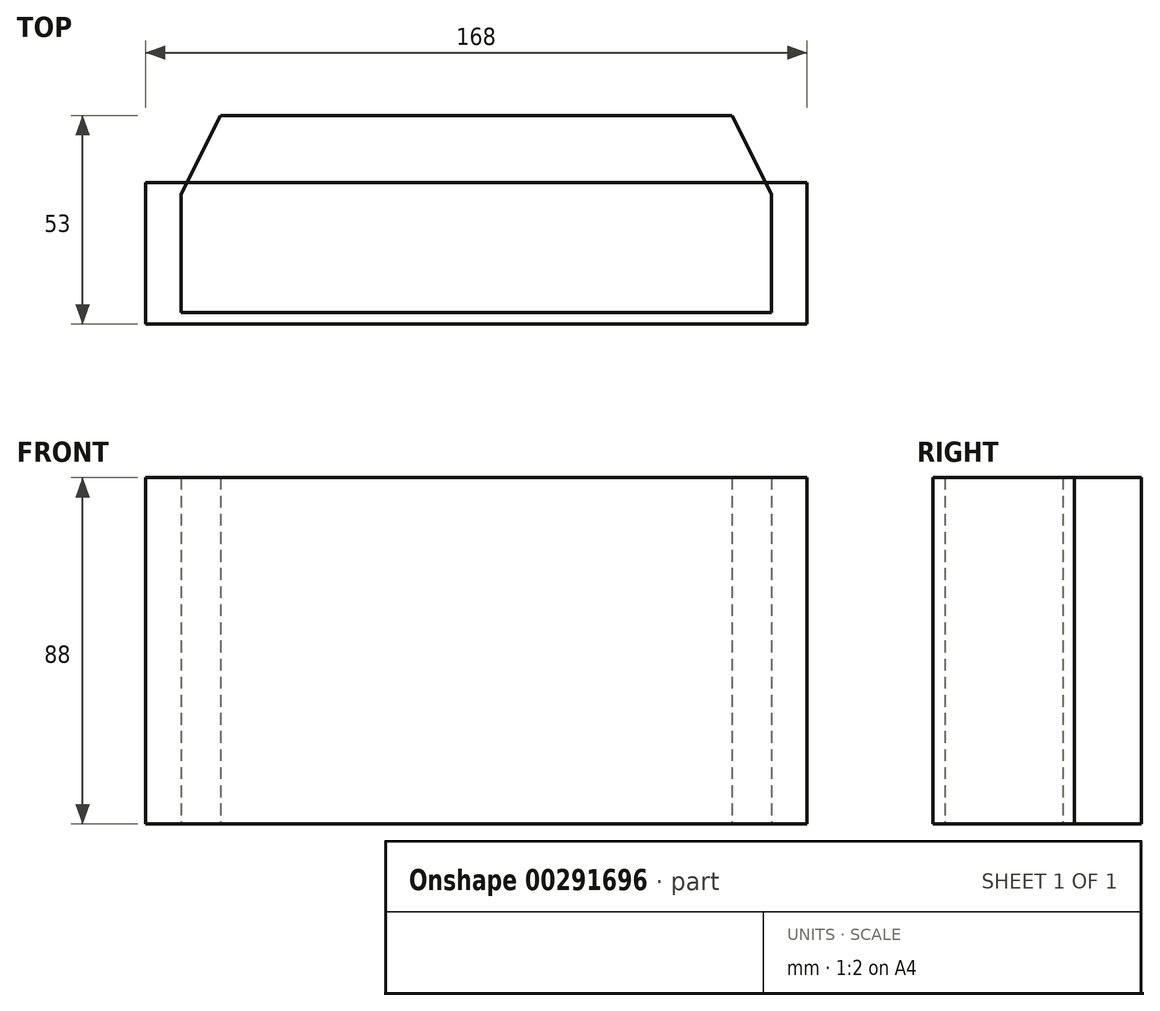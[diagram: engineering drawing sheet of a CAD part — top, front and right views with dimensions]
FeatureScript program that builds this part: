
annotation { "Feature Type Name" : "Feature", "Feature Type Description" : "" }
export const myFeature = defineFeature(function(context is Context, id is Id, definition is map)
    precondition{}
    {
        {
            var Q0;
            Q0=qCreatedBy(makeId("Top.planeOp"),FACE);
            var sketch = newSketch(context, id + "F0", { "sketchPlane" : qUnion([Q0])});
            skLineSegment(sketch, "E0.bottom", {"start": v(84, -18) * mm, "end": v(-84, -18) * mm});
            skLineSegment(sketch, "E0.top", {"start": v(84, 18) * mm, "end": v(-84, 18) * mm});
            skLineSegment(sketch, "E0.left", {"start": v(84, -18) * mm, "end": v(84, 18) * mm});
            skLineSegment(sketch, "E0.right", {"start": v(-84, -18) * mm, "end": v(-84, 18) * mm});
            skPoint(sketch, "E0.middle", {"position": v(0, 0) * mm});
            skSolve(sketch);
        }
        {
            var Q0;
            Q0 = qSketchRegion(id + "F0", true);
            extrude(context, id + "F1", {"entities" : qUnion([Q0]), "depth" : 88 * mm});
        }
        {
            var Q0;
            Q0=qCreatedBy(makeId("Top.planeOp"),FACE);
            var sketch = newSketch(context, id + "F2", { "sketchPlane" : qUnion([Q0])});
            skLineSegment(sketch, "E1.bottom", {"start": v(75, -15) * mm, "end": v(-75, -15) * mm});
            skLineSegment(sketch, "E1.left", {"start": v(75, -15) * mm, "end": v(75, 15) * mm});
            skLineSegment(sketch, "E1.right", {"start": v(-75, -15) * mm, "end": v(-75, 15) * mm});
            skPoint(sketch, "E1.middle", {"position": v(0, 0) * mm});
            skLineSegment(sketch, "E2", {"start": v(-75, 15) * mm, "end": v(-65, 35) * mm});
            skLineSegment(sketch, "E3", {"start": v(-65, 35) * mm, "end": v(65, 35) * mm});
            skLineSegment(sketch, "E4", {"start": v(65, 35) * mm, "end": v(75, 15) * mm});
            skPoint(sketch, "E5", {"position": v(0, 35) * mm});
            skSolve(sketch);
        }
        {
            var Q0;
            Q0 = qSketchRegion(id + "F2", true);
            extrude(context, id + "F3", {"entities" : qUnion([Q0]), "depth" : 88 * mm});
        }
    });
